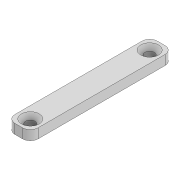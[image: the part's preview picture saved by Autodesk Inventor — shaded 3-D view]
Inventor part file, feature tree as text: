
AUTODESK INVENTOR PART (.ipt)
format: ipt  version: 2021 (Build 250183000, 183)  size: 103,424 bytes
history: native  units: mm
features: sketch x2, other x1, extrude x1, hole x1
ambient origin geometry x8: Origin, YZ Plane, XZ Plane, XY Plane, X Axis, Y Axis, Z Axis, Center Point
bodies: Body1 (feature_tree)
feature tree (5):
  other  "Твердое тело1"
  extrude  "Выдавливание1"  Depth=6.0mm
  hole  "Отверстие1"  [1 undecoded]
  sketch  "Эскиз1"
  sketch  "Эскиз2"
note: 1 required parameter value undecoded (feature->parameter linkage not recoverable at this tier; creation-order binding heuristic only, values carry confidence <= 0.55)
